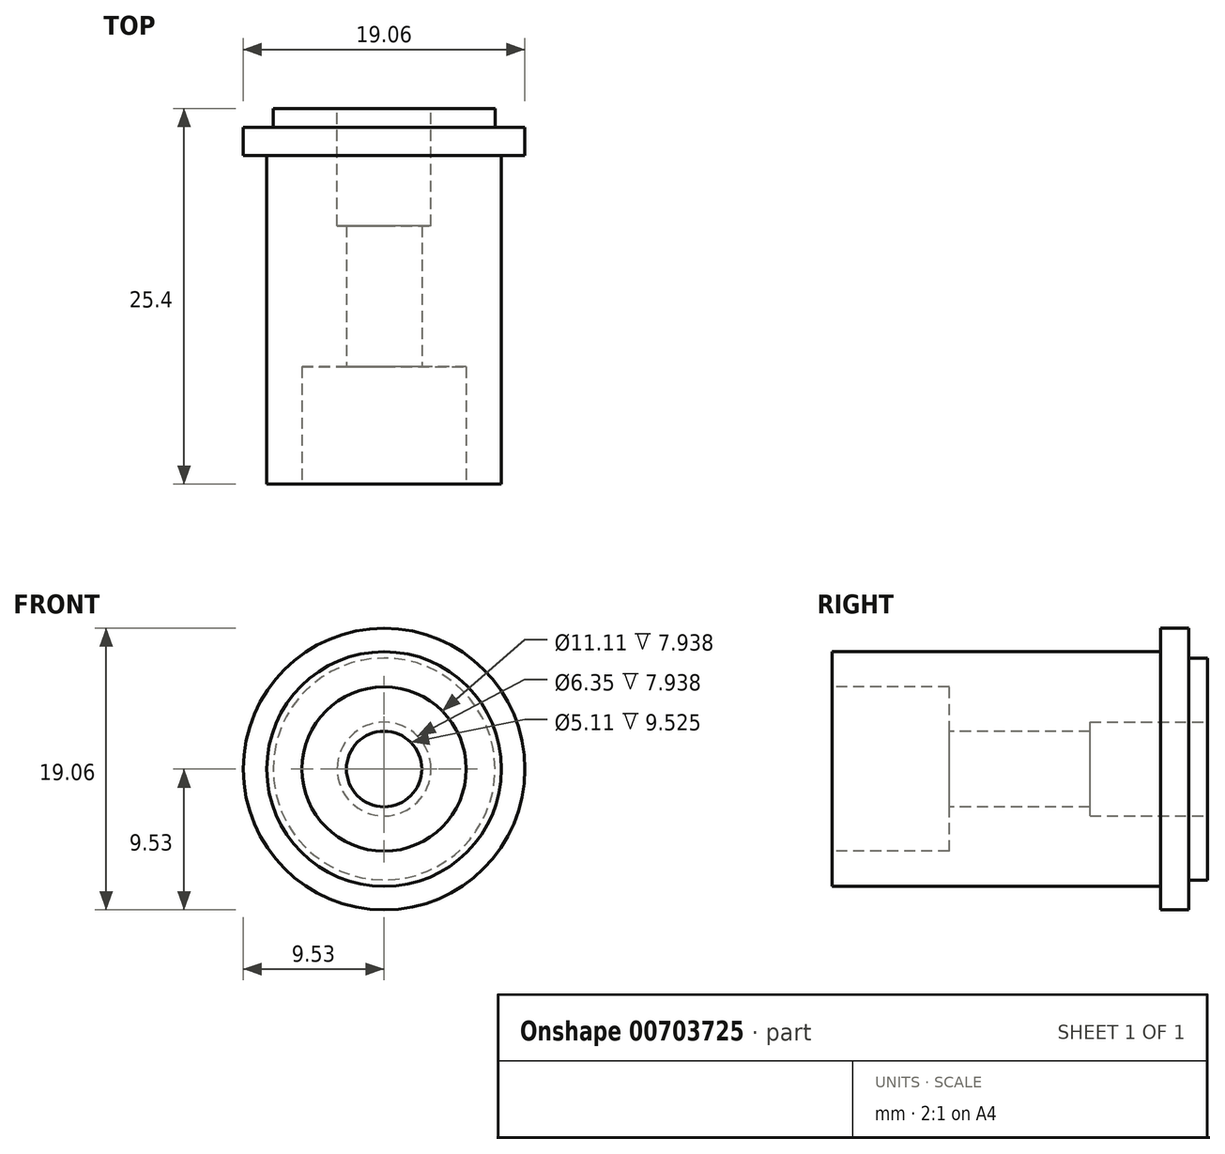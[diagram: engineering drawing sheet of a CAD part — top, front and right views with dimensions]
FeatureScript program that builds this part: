
annotation { "Feature Type Name" : "Feature", "Feature Type Description" : "" }
export const myFeature = defineFeature(function(context is Context, id is Id, definition is map)
    precondition{}
    {
        {
            var Q0;
            Q0=qCreatedBy(makeId("Front.planeOp"),FACE);
            var sketch = newSketch(context, id + "F0", { "sketchPlane" : qUnion([Q0])});
            skCircle(sketch, "E0", {"center": v(0, 0) * mm, "radius": 3.18 * mm});
            skCircle(sketch, "E1", {"center": v(0, 0) * mm, "radius": 9.53 * mm});
            skCircle(sketch, "E2", {"center": v(0, 0) * mm, "radius": 7.5 * mm});
            skSolve(sketch);
        }
        {
            var Q0;
            Q0=makeQuery(id+"F0.imprint","IMPRINT",FACE,{"disambiguationData":[TD([[makeQuery(id+"F0.imprint","IMPRINT",EDGE,{"derivedFrom":sQuery(id+"F0.wireOp",EDGE,"E1")}),1.0]])]});
            var Q1;
            Q1=makeQuery(id+"F0.imprint","IMPRINT",FACE,{"disambiguationData":[TD([[makeQuery(id+"F0.imprint","IMPRINT",EDGE,{"derivedFrom":sQuery(id+"F0.wireOp",EDGE,"E0")}),1.0]])]});
            var Q2;
            Q2=makeQuery(id+"F0.imprint","IMPRINT",FACE,{"disambiguationData":[TD([[makeQuery(id+"F0.imprint","IMPRINT",EDGE,{"derivedFrom":sQuery(id+"F0.wireOp",EDGE,"E0")}),-1.0]])]});
            extrude(context, id + "F1", {"entities" : qUnion([Q0, Q1, Q2]), "depth" : 25.4 * mm, "offsetDistance" : 25.4 * mm});
        }
        {
            var Q0;
            Q0=makeQuery(id+"F1.opExtrude","CAP_FACE",FACE,{"disambiguationData":[OSD([sQuery(id+"F0.wireOp",EDGE,"E1")])],"isStart":false});
            var sketch = newSketch(context, id + "F2", { "sketchPlane" : qUnion([Q0])});
            skCircle(sketch, "E3", {"center": v(0, 0) * mm, "radius": 5.56 * mm});
            skCircle(sketch, "E4", {"center": v(0, 0) * mm, "radius": 7.94 * mm});
            skSolve(sketch);
        }
        {
            var Q0;
            Q0=makeQuery(id+"F2.imprint","IMPRINT",FACE,{"disambiguationData":[TD([[makeQuery(id+"F2.imprint","IMPRINT",EDGE,{"derivedFrom":sQuery(id+"F2.wireOp",EDGE,"E3")}),1.0]])]});
            extrude(context, id + "F3", {"entities" : qUnion([Q0]), "operationType" : NewBodyOperationType.REMOVE, "oppositeDirection" : true, "depth" : 7.94 * mm, "offsetDistance" : 25.4 * mm});
        }
        {
            var Q0;
            Q0=makeQuery(id+"F3.boolean.opBoolean","COPY",FACE,{"derivedFrom":makeQuery(id+"F3.opExtrude","CAP_FACE",FACE,{"disambiguationData":[OSD([sQuery(id+"F2.wireOp",EDGE,"E3")])],"isStart":false})});
            var sketch = newSketch(context, id + "F4", { "sketchPlane" : qUnion([Q0])});
            skPoint(sketch, "E5", {"position": v(0, 0) * mm});
            skSolve(sketch);
        }
        {
            var Q0;
            Q0=makeQuery(id+"F2.imprint","IMPRINT",FACE,{"disambiguationData":[TD([[makeQuery(id+"F2.imprint","IMPRINT",EDGE,{"derivedFrom":sQuery(id+"F2.wireOp",EDGE,"E4")}),-1.0]])]});
            extrude(context, id + "F5", {"entities" : qUnion([Q0]), "operationType" : NewBodyOperationType.REMOVE, "oppositeDirection" : true, "depth" : 22.22 * mm, "offsetDistance" : 25.4 * mm});
        }
        {
            var Q0;
            Q0=makeQuery(id+"F0.imprint","IMPRINT",FACE,{"disambiguationData":[TD([[makeQuery(id+"F0.imprint","IMPRINT",EDGE,{"derivedFrom":sQuery(id+"F0.wireOp",EDGE,"E1")}),1.0]])]});
            extrude(context, id + "F6", {"entities" : qUnion([Q0]), "operationType" : NewBodyOperationType.REMOVE, "depth" : 1.27 * mm, "offsetDistance" : 25.4 * mm});
        }
        {
            var Q0;
            Q0=makeQuery(id+"F0.imprint","IMPRINT",FACE,{"disambiguationData":[TD([[makeQuery(id+"F0.imprint","IMPRINT",EDGE,{"derivedFrom":sQuery(id+"F0.wireOp",EDGE,"E0")}),1.0]])]});
            extrude(context, id + "F7", {"entities" : qUnion([Q0]), "operationType" : NewBodyOperationType.REMOVE, "depth" : 7.94 * mm, "offsetDistance" : 25.4 * mm});
        }
        {
            var Q0;
            Q0=sQuery(id+"F4.wireOp",VERTEX,"E5");
            var Q1;
            Q1=makeQuery(id+"F1.opExtrude","SWEPT_BODY",BODY,{"disambiguationData":[OSD([sQuery(id+"F0.wireOp",EDGE,"E1")])]});
            hole(context, id + "F8", {"style" : HoleStyle.SIMPLE, "endStyle" : HoleEndStyle.THROUGH, "holeDiameter" : 5.1 * mm, "majorDiameter" : 6.35 * mm, "isTappedThrough" : true, "tappedDepth" : 12.7 * mm, "tapClearance" : 3, "locations" : qUnion([Q0]), "scope" : qUnion([Q1])});
        }
    });
